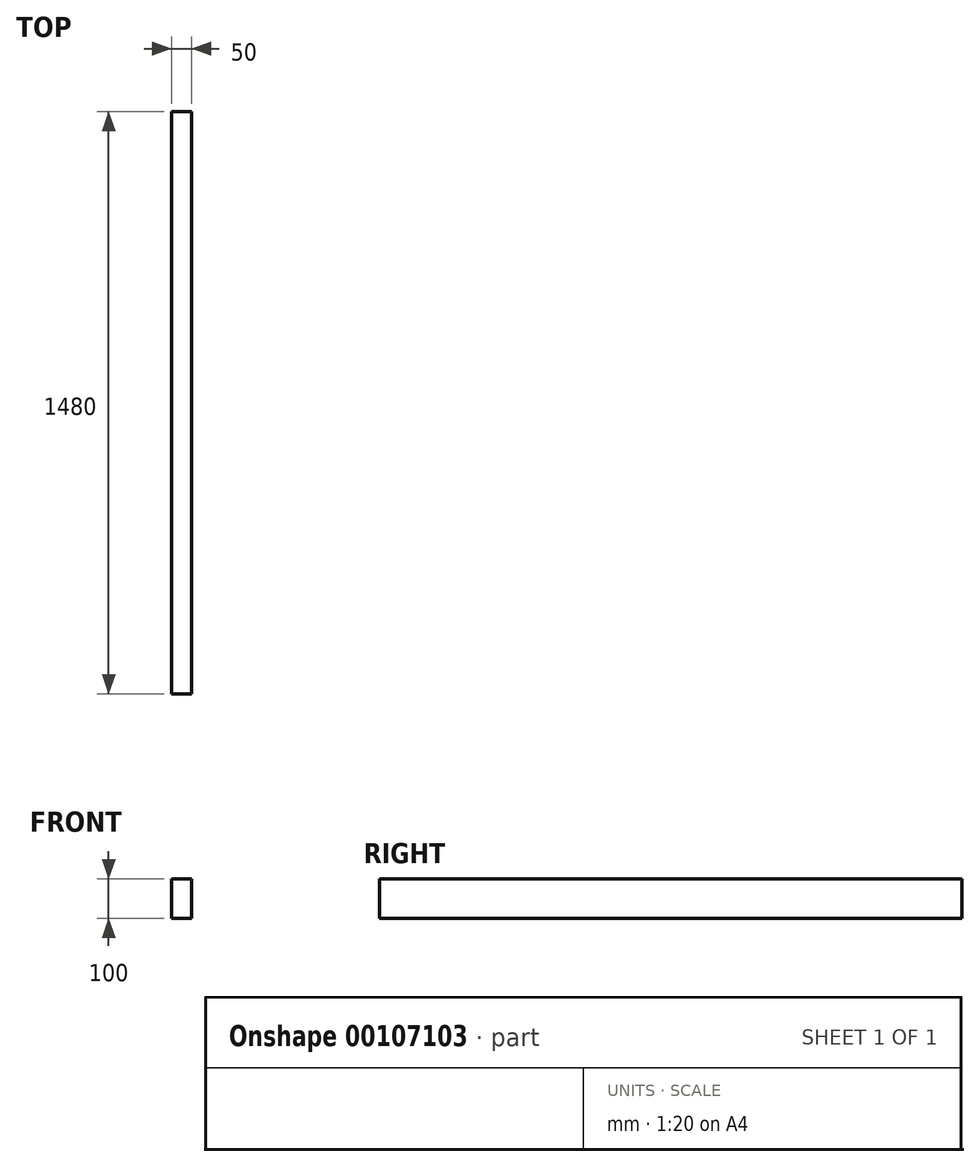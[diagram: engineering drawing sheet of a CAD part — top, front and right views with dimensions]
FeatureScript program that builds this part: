
annotation { "Feature Type Name" : "Feature", "Feature Type Description" : "" }
export const myFeature = defineFeature(function(context is Context, id is Id, definition is map)
    precondition{}
    {
        {
            var Q0;
            Q0=qCreatedBy(makeId("Front.planeOp"),FACE);
            var sketch = newSketch(context, id + "F0", { "sketchPlane" : qUnion([Q0])});
            skLineSegment(sketch, "E0.bottom", {"start": v(0, 0) * mm, "end": v(50, 0) * mm});
            skLineSegment(sketch, "E0.top", {"start": v(0, 100) * mm, "end": v(50, 100) * mm});
            skLineSegment(sketch, "E0.left", {"start": v(0, 0) * mm, "end": v(0, 100) * mm});
            skLineSegment(sketch, "E0.right", {"start": v(50, 0) * mm, "end": v(50, 100) * mm});
            skSolve(sketch);
        }
        {
            var Q0;
            Q0 = qSketchRegion(id + "F0", true);
            extrude(context, id + "F1", {"entities" : qUnion([Q0]), "depth" : 1480 * mm});
        }
    });
